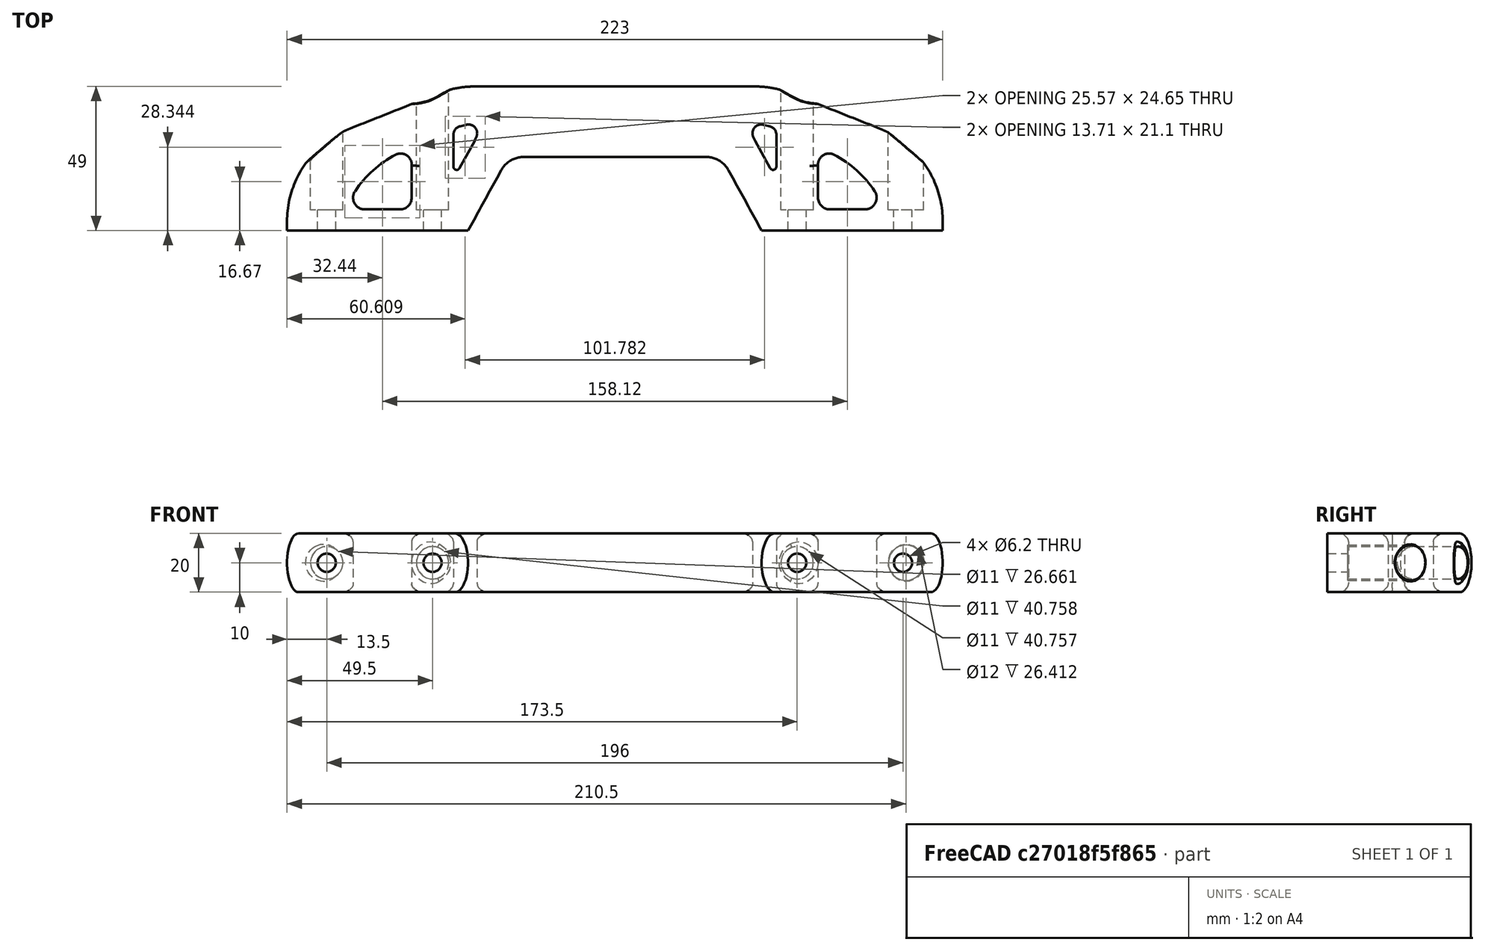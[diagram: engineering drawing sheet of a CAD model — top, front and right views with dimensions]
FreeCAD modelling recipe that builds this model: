
FCSTD DOCUMENT  (FreeCAD 0.17R9796 (Git))
Label: boxhandle1j
License: All rights reserved
LicenseURL: http://en.wikipedia.org/wiki/All_rights_reserved
objects: Part::Cylinder×8, Part::Cut×8, Part::Feature×2, TechDraw::DrawViewDimension×2, TechDraw::DrawSVGTemplate×1, TechDraw::DrawProjGroupItem×1, TechDraw::DrawProjGroup×1, TechDraw::DrawPage×1
note: 18 computed .brp shape members not serialized (recipe doc carries the construction recipe); baked Part::Feature solids carry a one-line shape summary decoded from their .brp

FEATURE [Part::Feature] Part__Feature  label="UltiHandleHD"
  shape: bbox 223 x 50.93 x 20 mm, 232 faces (baked)
FEATURE [Part::Cylinder] Cylinder  label="Zylinder"
  Angle = 360
  AttacherType = Attacher::AttachEngine3D
  Height = 50
  Placement = pos=(-62,7,7.5) rot=(-1,0,0;1.5708rad)
  Radius = 5.5
FEATURE [Part::Cylinder] Cylinder001  label="Zylinder001"
  Angle = 360
  AttacherType = Attacher::AttachEngine3D
  Height = 50
  Placement = pos=(62,7,7.5) rot=(-1,0,0;1.5708rad)
  Radius = 5.5
FEATURE [Part::Cylinder] Cylinder003  label="Zylinder003"
  Angle = 360
  AttacherType = Attacher::AttachEngine3D
  Height = 50
  Placement = pos=(-98,7,7.5) rot=(-1,0,0;1.5708rad)
  Radius = 5.5
FEATURE [Part::Cylinder] Cylinder004  label="Zylinder004"
  Angle = 360
  AttacherType = Attacher::AttachEngine3D
  Height = 50
  Placement = pos=(-62,-20,7.5) rot=(-1,0,0;1.5708rad)
  Radius = 3.1
FEATURE [Part::Cylinder] Cylinder005  label="Zylinder005"
  Angle = 360
  AttacherType = Attacher::AttachEngine3D
  Height = 50
  Placement = pos=(-98,-20,7.5) rot=(-1,0,0;1.5708rad)
  Radius = 3.1
FEATURE [Part::Cylinder] Cylinder006  label="Zylinder006"
  Angle = 360
  AttacherType = Attacher::AttachEngine3D
  Height = 50
  Placement = pos=(62,-20,7.5) rot=(-1,0,0;1.5708rad)
  Radius = 3.1
FEATURE [Part::Cylinder] Cylinder007  label="Zylinder007"
  Angle = 360
  AttacherType = Attacher::AttachEngine3D
  Height = 50
  Placement = pos=(98,-20,7.5) rot=(-1,0,0;1.5708rad)
  Radius = 3.1
FEATURE [Part::Cut] Cut
  Base = -> Part__Feature
  Tool = -> Cylinder
FEATURE [Part::Cut] Cut001
  Base = -> Cut
  Tool = -> Cylinder001
FEATURE [Part::Cut] Cut002
  Base = -> Cut001
  Tool = -> Cylinder003
FEATURE [Part::Cut] Cut003
  Base = -> Cut002
  Tool = -> Cylinder004
FEATURE [Part::Cut] Cut004
  Base = -> Cut003
  Tool = -> Cylinder005
FEATURE [Part::Cut] Cut005
  Base = -> Cut004
  Tool = -> Cylinder006
FEATURE [Part::Cut] Cut006
  Base = -> Cut005
  Tool = -> Cylinder007
FEATURE [Part::Cylinder] Cylinder008  label="Zylinder008"
  Angle = 360
  AttacherType = Attacher::AttachEngine3D
  Height = 50
  Placement = pos=(99,7,7.5) rot=(-1,0,0;1.5708rad)
  Radius = 6
FEATURE [Part::Cut] Cut007
  Base = -> Cut006
  Tool = -> Cylinder008
FEATURE [TechDraw::DrawSVGTemplate] Template
  Height = 210
  Orientation = 1
  Width = 297
FEATURE [TechDraw::DrawProjGroupItem] ProjItem  label="Front"
  ArcCenterMarks = true
  CenterScale = 2
  Direction = (0,-1,0)
  HardHidden = false
  HiddenWidth = 0.15
  HorizCenterLine = false
  IsoCount = 0
  IsoHidden = false
  IsoVisible = false
  IsoWidth = 0.3
  KeepLabel = false
  LineWidth = 0.7
  Rotation = 0
  RotationVector = (1,0,0)
  ScaleType = 0
  SeamHidden = false
  SeamVisible = false
  ShowSectionLine = true
  SmoothHidden = false
  SmoothVisible = false
  Source = -> Cut007
  Type = 0
  VertCenterLine = false
  X = 105.667
  Y = 219.26
FEATURE [TechDraw::DrawProjGroup] cView
  Anchor = -> ProjItem
  AutoDistribute = true
  KeepLabel = false
  ProjectionType = 0
  Rotation = 0
  ScaleType = 0
  Source = -> Cut007
  Views = -> [ProjItem]
  X = 150.441
  Y = 134.118
  spacingX = 15
  spacingY = 15
FEATURE [TechDraw::DrawViewDimension] Dimension
  Font = osifont
  Fontsize = 4
  FormatSpec = %value%
  KeepLabel = false
  LineWidth = 0.5
  MeasureType = 1
  References2D = -> [ProjItem]
  Rotation = 0
  ScaleType = 0
  Type = 1
  X = -79.1977
  Y = 22.4674
FEATURE [TechDraw::DrawViewDimension] Dimension001
  Font = osifont
  Fontsize = 4
  FormatSpec = %value%
  KeepLabel = false
  LineWidth = 0.5
  MeasureType = 1
  References2D = -> [ProjItem]
  Rotation = 0
  ScaleType = 0
  Type = 1
  X = -0.780119
  Y = -39.318
FEATURE [TechDraw::DrawPage] Page
  ProjectionType = 0
  Template = -> Template
  Views = -> [cView,Dimension,Dimension001]
FEATURE [Part::Feature] Cut007001  label="Cut008"
  shape: bbox 223 x 50.93 x 20 mm, 233 faces (baked)
